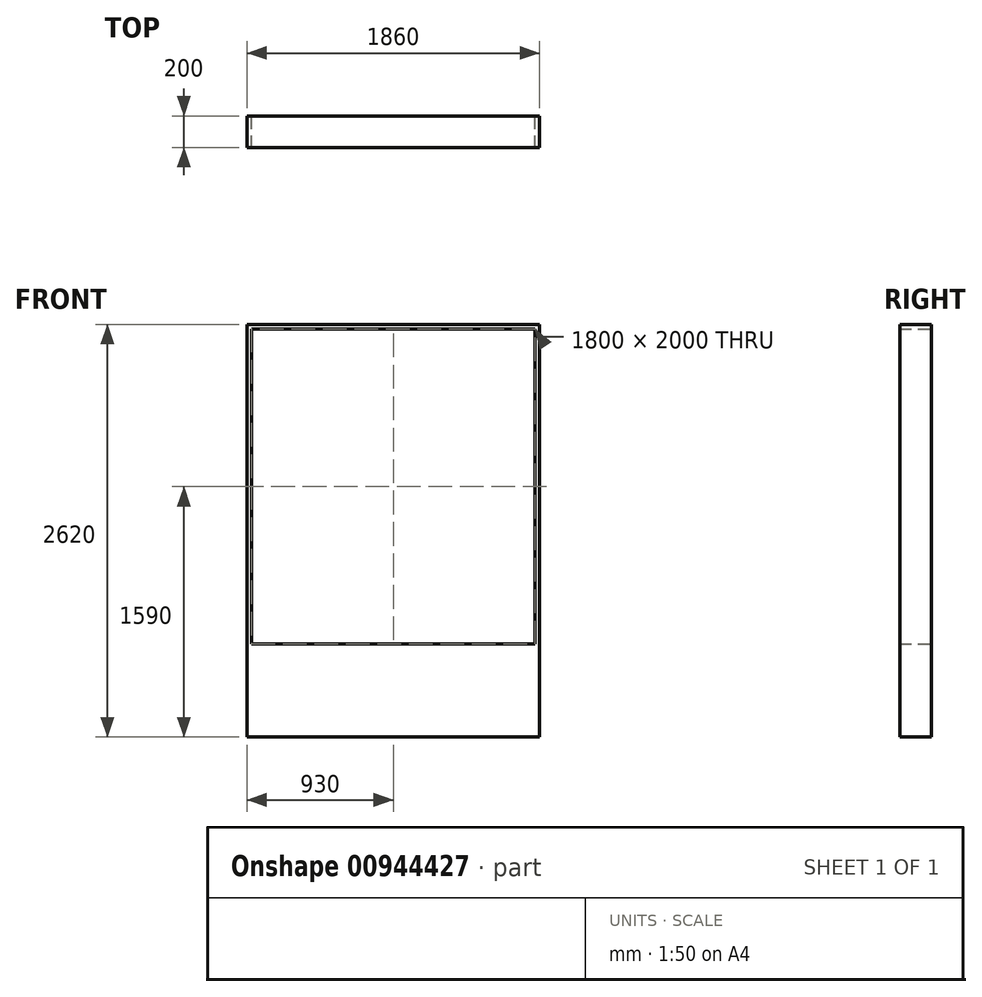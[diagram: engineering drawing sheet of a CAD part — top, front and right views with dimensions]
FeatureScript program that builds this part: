
annotation { "Feature Type Name" : "Feature", "Feature Type Description" : "" }
export const myFeature = defineFeature(function(context is Context, id is Id, definition is map)
    precondition{}
    {
        {
            var Q0;
            Q0=qCreatedBy(makeId("Front.planeOp"),FACE);
            var sketch = newSketch(context, id + "F0", { "sketchPlane" : qUnion([Q0])});
            skLineSegment(sketch, "E0.bottom", {"start": v(900, 1000) * mm, "end": v(-900, 1000) * mm});
            skLineSegment(sketch, "E0.top", {"start": v(900, -1000) * mm, "end": v(-900, -1000) * mm});
            skLineSegment(sketch, "E0.left", {"start": v(900, 1000) * mm, "end": v(900, -1000) * mm});
            skLineSegment(sketch, "E0.right", {"start": v(-900, 1000) * mm, "end": v(-900, -1000) * mm});
            skPoint(sketch, "E0.middle", {"position": v(0, 0) * mm});
            skLineSegment(sketch, "E1.bottom", {"start": v(930, 1030) * mm, "end": v(-930, 1030) * mm});
            skLineSegment(sketch, "E1.top", {"start": v(930, -1030) * mm, "end": v(-930, -1030) * mm});
            skLineSegment(sketch, "E1.left", {"start": v(930, 1030) * mm, "end": v(930, -1030) * mm});
            skLineSegment(sketch, "E1.right", {"start": v(-930, 1030) * mm, "end": v(-930, -1030) * mm});
            skLineSegment(sketch, "E2.bottom", {"start": v(-930, -1030) * mm, "end": v(930, -1030) * mm});
            skLineSegment(sketch, "E2.top", {"start": v(-930, -1590) * mm, "end": v(930, -1590) * mm});
            skLineSegment(sketch, "E2.left", {"start": v(-930, -1030) * mm, "end": v(-930, -1590) * mm});
            skLineSegment(sketch, "E2.right", {"start": v(930, -1030) * mm, "end": v(930, -1590) * mm});
            skSolve(sketch);
        }
        {
            var Q0;
            Q0 = qSketchRegion(id + "F0", true);
            extrude(context, id + "F1", {"entities" : qUnion([Q0]), "depth" : 200 * mm, "offsetDistance" : 25 * mm});
        }
    });
